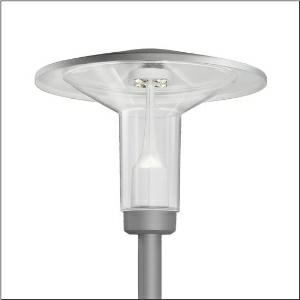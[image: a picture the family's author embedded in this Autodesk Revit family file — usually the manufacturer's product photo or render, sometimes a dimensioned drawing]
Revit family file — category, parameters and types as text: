
# Revit family: laterne_iq___pl1_2s_5xa5255of14h_60dd
name_source: partatom
category: Lighting Fixtures
units: mm (PartAtom-declared; Revit-internal decimal feet)

## family parameters
Cut with Voids When Loaded = No
Host = Face
Light Source = No
Part Type = Normal
Room Calculation Point = No
Round Connector Dimension = Use Diameter
Shared = No

## types (1)
- --- (1 x LED, 2970 lm, 21.8 W, 2700K)
    Apparent Load = 22 VA
    CIE Flux Codes = 25 63 94 98 100
    Color Rendering = 70
    Color Temperature = 2700K
    Default Elevation = 1800 mm
    Description = Lantern iQ, mast luminaire, Module 540 iQ-SR, primary light control with 3 zone facetted reflector, of plastic, silver coated, highly specular, structured, primary optical cover: cover, of PMMA, transparent, light distribution: PL1.2s, light emission: direct distribution, primary light characteristic: symmetric, installation type: post-top, LED, High Power LED, rated luminous flux: 2.970lm, luminous efficacy: 136lm/W, light colour: 727, colour temperature: 2700K, control gear: iQ Street-Remote, control: pre-setting: logarithmic dimming characteristic, Street-Remote, Auto-Match, Temp-Guard, Lumen-Switch, Night-Set, Smart-Wire, Light-Fading, Desk-Remote (wireless, voltage-free reading and setting of iQ features in the workshop via application-optimized NFC function/RFID function), optimised constant luminous flux control (CLO 2.0), with terminal, 6-pole, max. 2.5mm², mains connection: 230..240V, AC, 50/60Hz, start of lifetime: 22W, end of service life: 23W, reduction: 11W, luminaire housing, upper part, of glass-fibre reinforced polyester, coated, Siteco® metallic grey (DB 702S), diameter: 750mm, height: 583mm, spigot size: d x l = 76 x 70mm (post-top) | with reducer (optional accessory) 60 x 70mm, mounting height: 3..5m, post-top mast mounting element, of diecast aluminium, coated, Siteco® metallic grey (DB 702S), Module 540 iQ-SR, traffic white (RAL 9016), equipment: standard, protection rating (complete): IP65, insulation class (complete): insulation class II (safety insulation), certification: CE, ENEC, VDE, packaging unit: 1 piece

Light Distribution: PL1.2s
    Height = 583 mm
    Lamp = 1 x LED
    Lamp Light Flux = 2970 lm
    Lamp Power = 21.8 W
    Lamp count = 1
    Length = 750 mm
    Luminous efficacy = 136 lm/W
    Manufacturer = Siteco
    ModVariant = No
    Model = 5XA5255OF14H
    Number of Poles = 1
    OnlyDefault = Yes
    Power Factor = 1
    Product Name = Laterne iQ | PL1.2s
    Product group = mast luminaire | pylon top
    ProductGroupID = 6100
    Protection Class = Protection class II
    Protection Degree = IP 65
    RLX_Detail_Level = 1
    RLX_Emergency_Light_Flux = 0 lm
    RLX_Emergency_Type = 0
    RLX_Emergency_Type_DB = No
    RlxData = <blob elided: 31589 chars, md5=5b12a406>
    Socket = socket
    Standby Power = 0 W
    System Light Flux = 2970 lm
    System Power = 22 W
    Type Comments = factory setting: luminous flux: 100 % | dim-lin: 254 | 456 mA
    Type Image = l_1006050.jpg
    URL = http://relux.com
    VarID = @adj_145814
    Voltage = 0 V
    Weight = 0.00 kg
    Width = 0 mm  [stored 0 ft]

note: [stored X ft] marks values corroborated as IEEE doubles in the binary element streams (Revit-internal decimal feet)

## geometry (parser evidence)
native form markers: Blend x4, Sweep x9
no freeform markers — native parametric forms only
